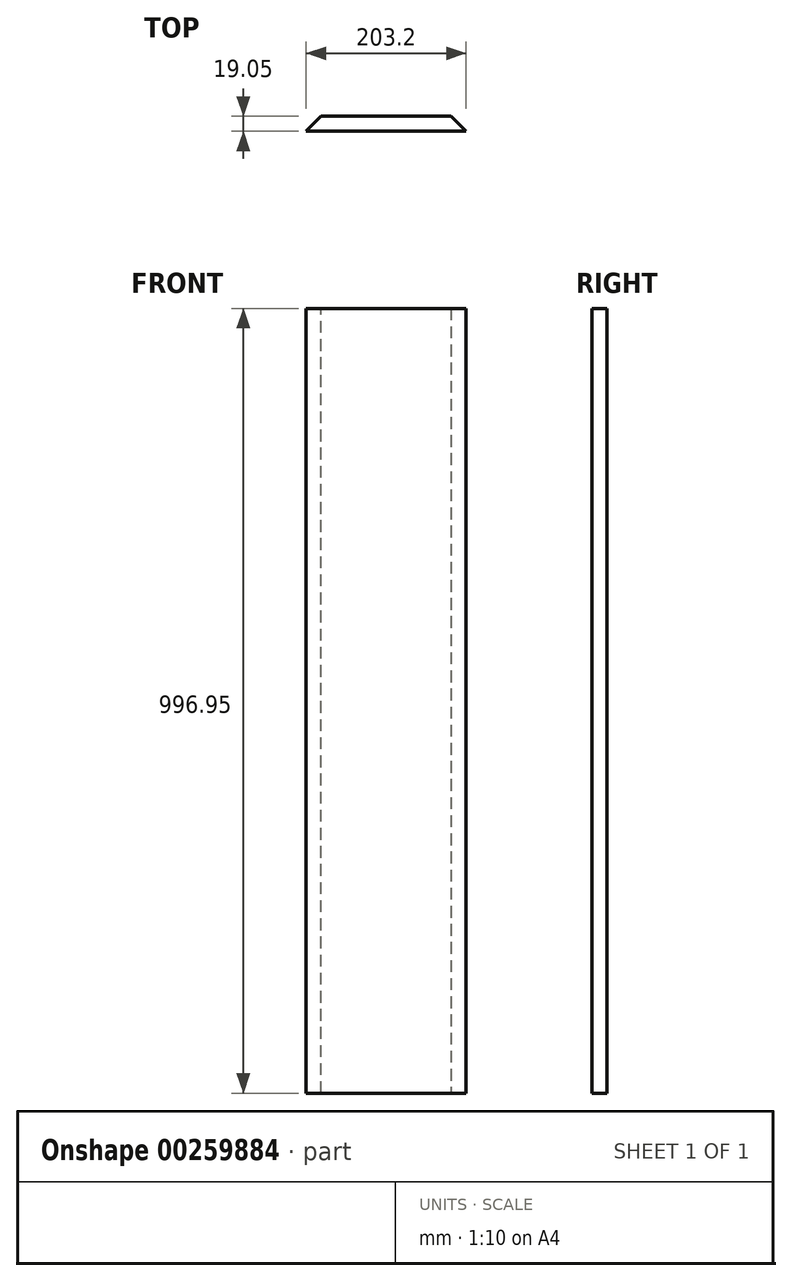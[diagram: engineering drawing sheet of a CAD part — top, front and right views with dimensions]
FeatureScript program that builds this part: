
annotation { "Feature Type Name" : "Feature", "Feature Type Description" : "" }
export const myFeature = defineFeature(function(context is Context, id is Id, definition is map)
    precondition{}
    {
        {
            var Q0;
            Q0=qCreatedBy(makeId("Front.planeOp"),FACE);
            var sketch = newSketch(context, id + "F0", { "sketchPlane" : qUnion([Q0])});
            skLineSegment(sketch, "E0.bottom", {"start": v(-101.6, 476.15) * mm, "end": v(101.6, 476.15) * mm});
            skLineSegment(sketch, "E0.top", {"start": v(-101.6, -520.8) * mm, "end": v(101.6, -520.8) * mm});
            skLineSegment(sketch, "E0.left", {"start": v(-101.6, 476.15) * mm, "end": v(-101.6, -520.8) * mm});
            skLineSegment(sketch, "E0.right", {"start": v(101.6, 476.15) * mm, "end": v(101.6, -520.8) * mm});
            skSolve(sketch);
        }
        {
            var Q0;
            Q0=makeQuery(id+"F0.imprint","IMPRINT",FACE,{"disambiguationData":[TD([[makeQuery(id+"F0.imprint","IMPRINT",EDGE,{"derivedFrom":sQuery(id+"F0.wireOp",EDGE,"E0.bottom")}),-1.0]])]});
            extrude(context, id + "F1", {"entities" : qUnion([Q0]), "depth" : 19.05 * mm});
        }
        {
            var Q0;
            Q0=makeQuery(id+"F1.opExtrude","CAP_EDGE",EDGE,{"disambiguationData":[OSD([sQuery(id+"F0.wireOp",EDGE,"E0.left")])],"isStart":true});
            var Q1;
            Q1=makeQuery(id+"F1.opExtrude","CAP_EDGE",EDGE,{"disambiguationData":[OSD([sQuery(id+"F0.wireOp",EDGE,"E0.right")])],"isStart":true});
            chamfer(context, id + "F2", {"entities" : qUnion([Q0, Q1]), "chamferType" : ChamferType.OFFSET_ANGLE, "width" : 19.05 * mm, "oppositeDirection" : false, "angle" : 45 * degree, "tangentPropagation" : true});
        }
    });
